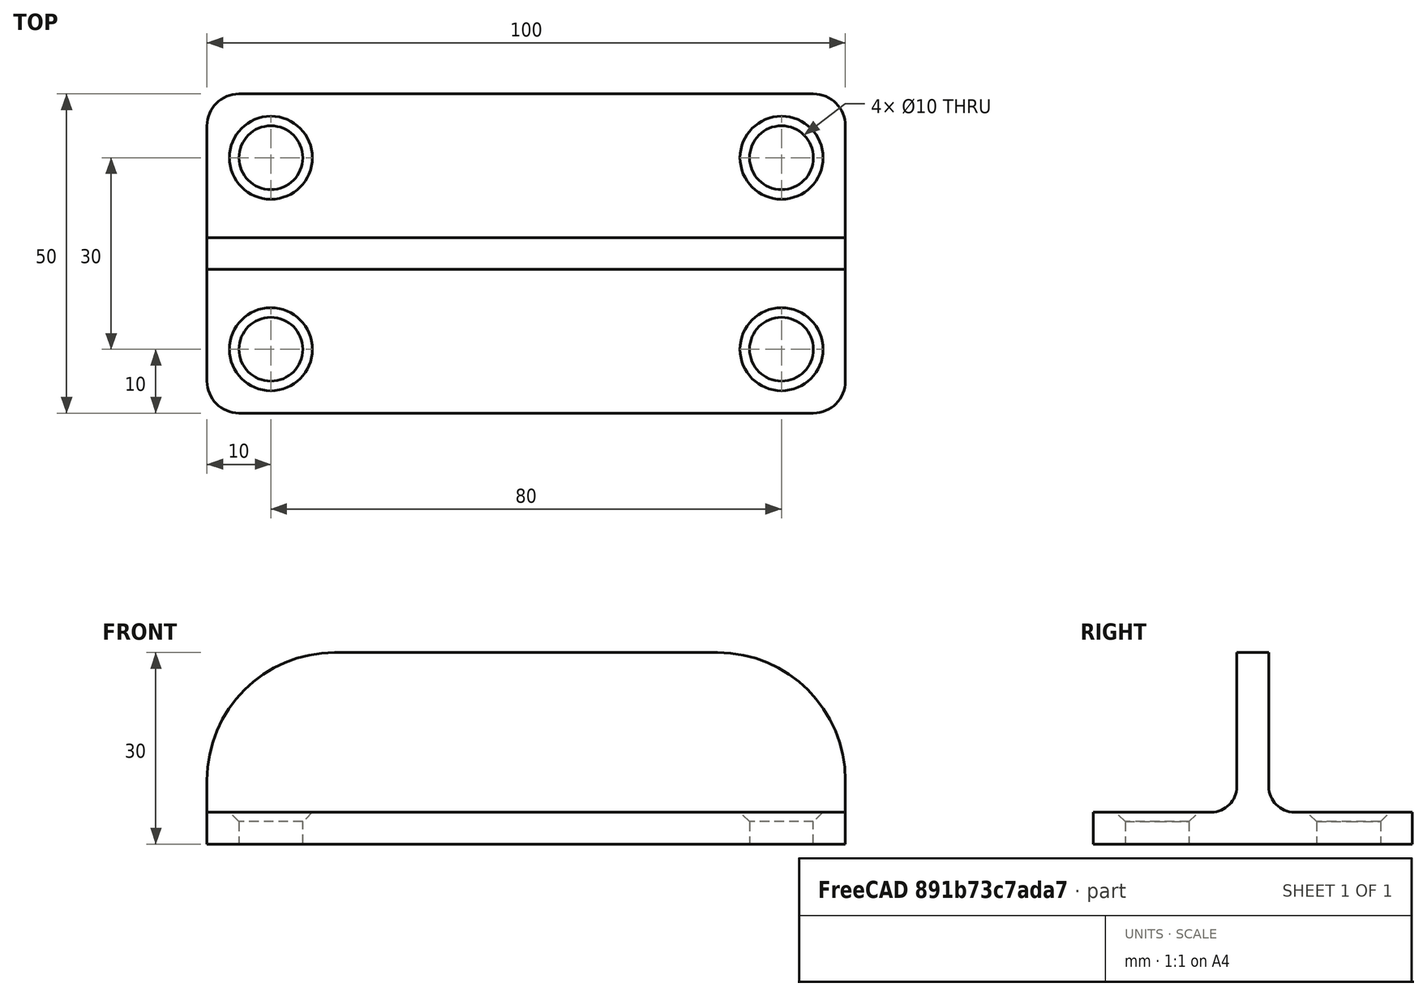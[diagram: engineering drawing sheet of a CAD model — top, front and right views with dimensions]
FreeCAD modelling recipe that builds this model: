
FCSTD DOCUMENT  (FreeCAD 0.20R29410 (Git))
Label: MangoJelly_Solutions_Tutorial_Ep3
License: All rights reserved
LicenseURL: http://en.wikipedia.org/wiki/All_rights_reserved
objects: TechDraw::DrawViewDimension×8, TechDraw::DrawProjGroupItem×3, Sketcher::SketchObject×2, PartDesign::Pad×2, PartDesign::Fillet×1, PartDesign::Chamfer×1, PartDesign::Body×1, TechDraw::DrawSVGTemplate×1, TechDraw::DrawViewPart×1, TechDraw::DrawProjGroup×1, TechDraw::DrawViewAnnotation×1, TechDraw::DrawPage×1
note: 11 computed .brp shape members not serialized (recipe doc carries the construction recipe); baked Part::Feature solids carry a one-line shape summary decoded from their .brp

FEATURE [Sketcher::SketchObject] Sketch
  FullyConstrained = true
  MapMode = 5
  Support = -> [XY_Plane]
  sketch-geometry (17):
    g0: LineSegment StartX=-50 StartY=20 StartZ=0 EndX=-50 EndY=-20 EndZ=0
    g1: LineSegment StartX=-45 StartY=-25 StartZ=0 EndX=45 EndY=-25 EndZ=0
    g2: LineSegment StartX=50 StartY=-20 StartZ=0 EndX=50 EndY=20 EndZ=0
    g3: LineSegment StartX=45 StartY=25 StartZ=0 EndX=-45 EndY=25 EndZ=0
    g4: GeomPoint X=0 Y=0 Z=0
    g5: Circle CenterX=-40 CenterY=15 CenterZ=0 NormalX=0 NormalY=0 NormalZ=1 AngleXU=0 Radius=5
    g6: Circle CenterX=-40 CenterY=-15 CenterZ=0 NormalX=0 NormalY=0 NormalZ=1 AngleXU=0 Radius=5
    g7: Circle CenterX=40 CenterY=-15 CenterZ=0 NormalX=0 NormalY=0 NormalZ=1 AngleXU=0 Radius=5
    g8: Circle CenterX=40 CenterY=15 CenterZ=0 NormalX=0 NormalY=0 NormalZ=1 AngleXU=0 Radius=5
    g9: ArcOfCircle CenterX=-45 CenterY=20 CenterZ=0 NormalX=0 NormalY=0 NormalZ=1 AngleXU=0 Radius=5 StartAngle=1.5708 EndAngle=3.14159
    g10: GeomPoint X=-50 Y=25 Z=0
    g11: ArcOfCircle CenterX=45 CenterY=20 CenterZ=0 NormalX=0 NormalY=0 NormalZ=1 AngleXU=0 Radius=5 StartAngle=9e-15 EndAngle=1.5708
    g12: GeomPoint X=50 Y=25 Z=0
    g13: ArcOfCircle CenterX=45 CenterY=-20 CenterZ=0 NormalX=0 NormalY=0 NormalZ=1 AngleXU=0 Radius=5 StartAngle=4.71239 EndAngle=6.28319
    g14: GeomPoint X=50 Y=-25 Z=0
    g15: ArcOfCircle CenterX=-45 CenterY=-20 CenterZ=0 NormalX=0 NormalY=0 NormalZ=1 AngleXU=0 Radius=5 StartAngle=3.14159 EndAngle=4.71239
    g16: GeomPoint X=-50 Y=-25 Z=0
  constraints (38):
    c: Horizontal(g1)
    c: Horizontal(g3)
    c: Vertical(g0)
    c: Vertical(g2)
    c: Symmetric(g14,g10,g4)
    c: Coincident(g4,g-1)
    c: DistanceX(g10,g12) = 100
    c: DistanceY(g14,g12) = 50
    c: Diameter(g5) = 10
    c: Equal(g8,g7)
    c: Equal(g7,g6)
    c: Equal(g6,g5)
    c: Symmetric(g5,g8,g-2)
    c: Symmetric(g5,g6,g-1)
    c: Vertical(g7,g8)
    c: Horizontal(g7,g6)
    c: DistanceX(g10,g5) = 10
    c: DistanceY(g5,g10) = 10
    c: PointOnObject(g10,g0)
    c: PointOnObject(g10,g3)
    c: Tangent(g0,g9) = -1.5708
    c: Tangent(g3,g9) = -1.5708
    c: PointOnObject(g12,g3)
    c: PointOnObject(g12,g2)
    c: Tangent(g3,g11) = -1.5708
    c: Tangent(g2,g11) = -1.5708
    c: Diameter(g9) = 10
    c: PointOnObject(g14,g1)
    c: PointOnObject(g14,g2)
    c: Tangent(g1,g13) = -1.5708
    c: Tangent(g2,g13) = -1.5708
    c: PointOnObject(g16,g1)
    c: PointOnObject(g16,g0)
    c: Tangent(g1,g15) = -1.5708
    c: Tangent(g0,g15) = -1.5708
    c: Equal(g13,g11)
    c: Equal(g11,g15)
    c: Equal(g15,g9)
FEATURE [PartDesign::Pad] Pad
  Direction = (0,0,1)
  Length = 5
  Length2 = 10
  Profile = -> Sketch
  ReferenceAxis = -> Sketch [N_Axis]
  Type = 0
FEATURE [Sketcher::SketchObject] Sketch001
  ExternalGeometry = -> [Pad]
  FullyConstrained = true
  MapMode = 5
  Placement = pos=(0,0,0) rot=(1,0,0;1.5708rad)
  Support = -> [XZ_Plane]
  sketch-geometry (8):
    g0: LineSegment StartX=-30 StartY=30 StartZ=0 EndX=30 EndY=30 EndZ=0
    g1: LineSegment StartX=50 StartY=10 StartZ=0 EndX=50 EndY=5 EndZ=0
    g2: LineSegment StartX=50 StartY=5 StartZ=0 EndX=-50 EndY=5 EndZ=0
    g3: LineSegment StartX=-50 StartY=5 StartZ=0 EndX=-50 EndY=10 EndZ=0
    g4: ArcOfCircle CenterX=-30 CenterY=10 CenterZ=0 NormalX=0 NormalY=0 NormalZ=1 AngleXU=0 Radius=20 StartAngle=1.5708 EndAngle=3.14159
    g5: GeomPoint X=-50 Y=30 Z=0
    g6: ArcOfCircle CenterX=30 CenterY=10 CenterZ=0 NormalX=0 NormalY=0 NormalZ=1 AngleXU=0 Radius=20 StartAngle=5.3e-15 EndAngle=1.5708
    g7: GeomPoint X=50 Y=30 Z=0
  constraints (18):
    c: Coincident(g1,g2)
    c: Coincident(g2,g3)
    c: Horizontal(g0)
    c: Vertical(g1)
    c: Vertical(g3)
    c: Coincident(g-3,g1)
    c: Coincident(g2,g-4)
    c: DistanceY(g1,g7) = 25
    c: PointOnObject(g5,g3)
    c: PointOnObject(g5,g0)
    c: Tangent(g3,g4) = 1.5708
    c: Tangent(g0,g4) = 1.5708
    c: PointOnObject(g7,g0)
    c: PointOnObject(g7,g1)
    c: Tangent(g0,g6) = 1.5708
    c: Tangent(g1,g6) = 1.5708
    c: Diameter(g4) = 40
    c: Equal(g6,g4)
FEATURE [PartDesign::Pad] Pad001
  BaseFeature = -> Pad
  Direction = (0,-1,2e-16)
  Length = 5
  Length2 = 10
  Midplane = true
  Profile = -> Sketch001
  ReferenceAxis = -> Sketch001 [N_Axis]
  Type = 0
FEATURE [PartDesign::Fillet] Fillet
  Base = -> Pad001 [Edge31,Edge25]
  BaseFeature = -> Pad001
  Radius = 4
  SupportTransform = false
  UseAllEdges = false
FEATURE [PartDesign::Chamfer] Chamfer
  Angle = 45
  Base = -> Fillet [Edge39,Edge14,Edge15,Edge40]
  BaseFeature = -> Fillet
  ChamferType = 0
  FlipDirection = false
  Size = 1.5
  Size2 = 1
  SupportTransform = false
  UseAllEdges = false
FEATURE [PartDesign::Body] Body
  Group = -> [Sketch,Pad,Sketch001,Pad001,Fillet,Chamfer]
  Origin = -> Origin
  Tip = -> Chamfer
FEATURE [TechDraw::DrawSVGTemplate] Template
  Height = 297
  Orientation = 0
  Width = 210
FEATURE [TechDraw::DrawViewPart] View001  label="View"
  Caption = 3D View
  CoarseView = false
  Direction = (0.563,-0.474,0.677)
  Focus = 100
  HardHidden = false
  IsoCount = 0
  IsoHidden = false
  IsoVisible = false
  LockPosition = false
  Perspective = false
  Rotation = 0
  ScaleType = 0
  SeamHidden = false
  SeamVisible = true
  SmoothHidden = false
  SmoothVisible = true
  Source = -> [Body]
  X = 61.0559
  XDirection = (0.738,0.657,-0.155)
  Y = 239.133
FEATURE [TechDraw::DrawProjGroupItem] ProjItem  label="Top"
  Caption = Top View
  CoarseView = false
  Direction = (0,0,1)
  Focus = 100
  HardHidden = false
  IsoCount = 0
  IsoHidden = false
  IsoVisible = false
  LockPosition = true
  Perspective = false
  Rotation = 0
  RotationVector = (1,0,0)
  ScaleType = 2
  SeamHidden = false
  SeamVisible = true
  SmoothHidden = false
  SmoothVisible = true
  Source = -> [Body]
  Type = 0
  X = 0
  XDirection = (1,0,0)
  Y = 0
FEATURE [TechDraw::DrawProjGroupItem] ProjItem001  label="Right"
  Caption = Left View
  CoarseView = false
  Direction = (1,0,1e-16)
  Focus = 100
  HardHidden = false
  IsoCount = 0
  IsoHidden = false
  IsoVisible = false
  LockPosition = false
  Perspective = false
  Rotation = -90
  RotationVector = (1,0,0)
  ScaleType = 2
  SeamHidden = false
  SeamVisible = true
  SmoothHidden = false
  SmoothVisible = true
  Source = -> [Body]
  Type = 2
  X = -115
  XDirection = (1e-16,0,-1)
  Y = 0
FEATURE [TechDraw::DrawProjGroupItem] ProjItem002  label="Front"
  Caption = Front View
  CoarseView = false
  Direction = (0,-1,0)
  Focus = 100
  HardHidden = false
  IsoCount = 0
  IsoHidden = false
  IsoVisible = false
  LockPosition = false
  Perspective = false
  Rotation = 0
  RotationVector = (1,0,0)
  ScaleType = 2
  SeamHidden = false
  SeamVisible = true
  SmoothHidden = false
  SmoothVisible = true
  Source = -> [Body]
  Type = 5
  X = 0
  XDirection = (1,0,0)
  Y = 65
FEATURE [TechDraw::DrawProjGroup] ProjGroup
  Anchor = -> ProjItem
  AutoDistribute = true
  LockPosition = false
  ProjectionType = 0
  Rotation = 0
  ScaleType = 0
  Source = -> [Body]
  Views = -> [ProjItem,ProjItem001,ProjItem002]
  X = 147.142
  Y = 69.2058
  spacingX = 15
  spacingY = 15
FEATURE [TechDraw::DrawViewDimension] Dimension
  AngleOverride = false
  Arbitrary = false
  ArbitraryTolerances = false
  EqualTolerance = true
  ExtensionAngle = 0
  FormatSpec = %.2w
  FormatSpecOverTolerance = %+.2w
  FormatSpecUnderTolerance = %+.2w
  Inverted = false
  LineAngle = 0
  LockPosition = false
  MeasureType = 1
  OverTolerance = 0
  References2D = -> [ProjItem]
  Rotation = 0
  ScaleType = 0
  TheoreticalExact = false
  Type = 2
  UnderTolerance = 0
  X = 56.1576
  Y = 2.44419
FEATURE [TechDraw::DrawViewDimension] Dimension001
  AngleOverride = false
  Arbitrary = false
  ArbitraryTolerances = false
  EqualTolerance = true
  ExtensionAngle = 0
  FormatSpec = %.2w
  FormatSpecOverTolerance = %+.2w
  FormatSpecUnderTolerance = %+.2w
  Inverted = false
  LineAngle = 0
  LockPosition = false
  MeasureType = 1
  OverTolerance = 0
  References2D = -> [ProjItem]
  Rotation = 0
  ScaleType = 0
  TheoreticalExact = false
  Type = 1
  UnderTolerance = 0
  X = 0.183585
  Y = -38.6723
FEATURE [TechDraw::DrawViewDimension] Dimension004
  AngleOverride = false
  Arbitrary = false
  ArbitraryTolerances = false
  EqualTolerance = true
  ExtensionAngle = 0
  FormatSpec = R%.2w
  FormatSpecOverTolerance = %+.2w
  FormatSpecUnderTolerance = %+.2w
  Inverted = false
  LineAngle = 0
  LockPosition = false
  MeasureType = 1
  OverTolerance = 0
  References2D = -> [ProjItem002]
  Rotation = 0
  ScaleType = 0
  TheoreticalExact = false
  Type = 4
  UnderTolerance = 0
  X = -60.567
  Y = 12.488
FEATURE [TechDraw::DrawViewDimension] Dimension005
  AngleOverride = false
  Arbitrary = false
  ArbitraryTolerances = false
  EqualTolerance = true
  ExtensionAngle = 0
  FormatSpec = %.2w
  FormatSpecOverTolerance = %+.2w
  FormatSpecUnderTolerance = %+.2w
  Inverted = false
  LineAngle = 0
  LockPosition = false
  MeasureType = 1
  OverTolerance = 0
  References2D = -> [ProjItem002]
  Rotation = 0
  ScaleType = 0
  TheoreticalExact = false
  Type = 2
  UnderTolerance = 0
  X = -63.5683
  Y = -17.1941
FEATURE [TechDraw::DrawViewDimension] Dimension006
  AngleOverride = false
  Arbitrary = false
  ArbitraryTolerances = false
  EqualTolerance = true
  ExtensionAngle = 0
  FormatSpec = %.2w
  FormatSpecOverTolerance = %+.2w
  FormatSpecUnderTolerance = %+.2w
  Inverted = false
  LineAngle = 0
  LockPosition = false
  MeasureType = 1
  OverTolerance = 0
  References2D = -> [ProjItem001]
  Rotation = 0
  ScaleType = 0
  TheoreticalExact = false
  Type = 2
  UnderTolerance = 0
  X = -16.0807
  Y = 4.48705
FEATURE [TechDraw::DrawViewDimension] Dimension007
  AngleOverride = false
  Arbitrary = false
  ArbitraryTolerances = false
  EqualTolerance = true
  ExtensionAngle = 0
  FormatSpec = %.2w
  FormatSpecOverTolerance = %+.2w
  FormatSpecUnderTolerance = %+.2w
  Inverted = false
  LineAngle = 0
  LockPosition = false
  MeasureType = 1
  OverTolerance = 0
  References2D = -> [ProjItem001]
  Rotation = 0
  ScaleType = 0
  TheoreticalExact = false
  Type = 1
  UnderTolerance = 0
  X = 9.05383
  Y = 31.1922
FEATURE [TechDraw::DrawViewDimension] Dimension008
  AngleOverride = false
  Arbitrary = false
  ArbitraryTolerances = false
  EqualTolerance = true
  ExtensionAngle = 0
  FormatSpec = ⌀%.2w
  FormatSpecOverTolerance = %+.2w
  FormatSpecUnderTolerance = %+.2w
  Inverted = false
  LineAngle = 0
  LockPosition = false
  MeasureType = 1
  OverTolerance = 0
  References2D = -> [ProjItem]
  Rotation = 0
  ScaleType = 0
  TheoreticalExact = false
  Type = 5
  UnderTolerance = 0
  X = -67.2909
  Y = -10.5464
FEATURE [TechDraw::DrawViewDimension] Dimension009
  AngleOverride = false
  Arbitrary = false
  ArbitraryTolerances = false
  EqualTolerance = true
  ExtensionAngle = 0
  FormatSpec = R%.2w
  FormatSpecOverTolerance = %+.2w
  FormatSpecUnderTolerance = %+.2w
  Inverted = false
  LineAngle = 0
  LockPosition = false
  MeasureType = 1
  OverTolerance = 0
  References2D = -> [ProjItem]
  Rotation = 0
  ScaleType = 0
  TheoreticalExact = false
  Type = 4
  UnderTolerance = 0
  X = -64.7007
  Y = -27.2518
FEATURE [TechDraw::DrawViewAnnotation] Annotation
  Font = osifont
  LineSpace = 80
  LockPosition = false
  MaxWidth = -1
  Rotation = 0
  ScaleType = 0
  Text = My First Model
  TextSize = 11
  TextStyle = 0
  X = 160.289
  Y = 231.75
FEATURE [TechDraw::DrawPage] Page
  KeepUpdated = true
  NextBalloonIndex = 1
  ProjectionType = 0
  Template = -> Template
  Views = -> [View001,ProjGroup,Dimension,Dimension001,Dimension004,Dimension005,Dimension006,Dimension007,Dimension008,Dimension009,Annotation]
